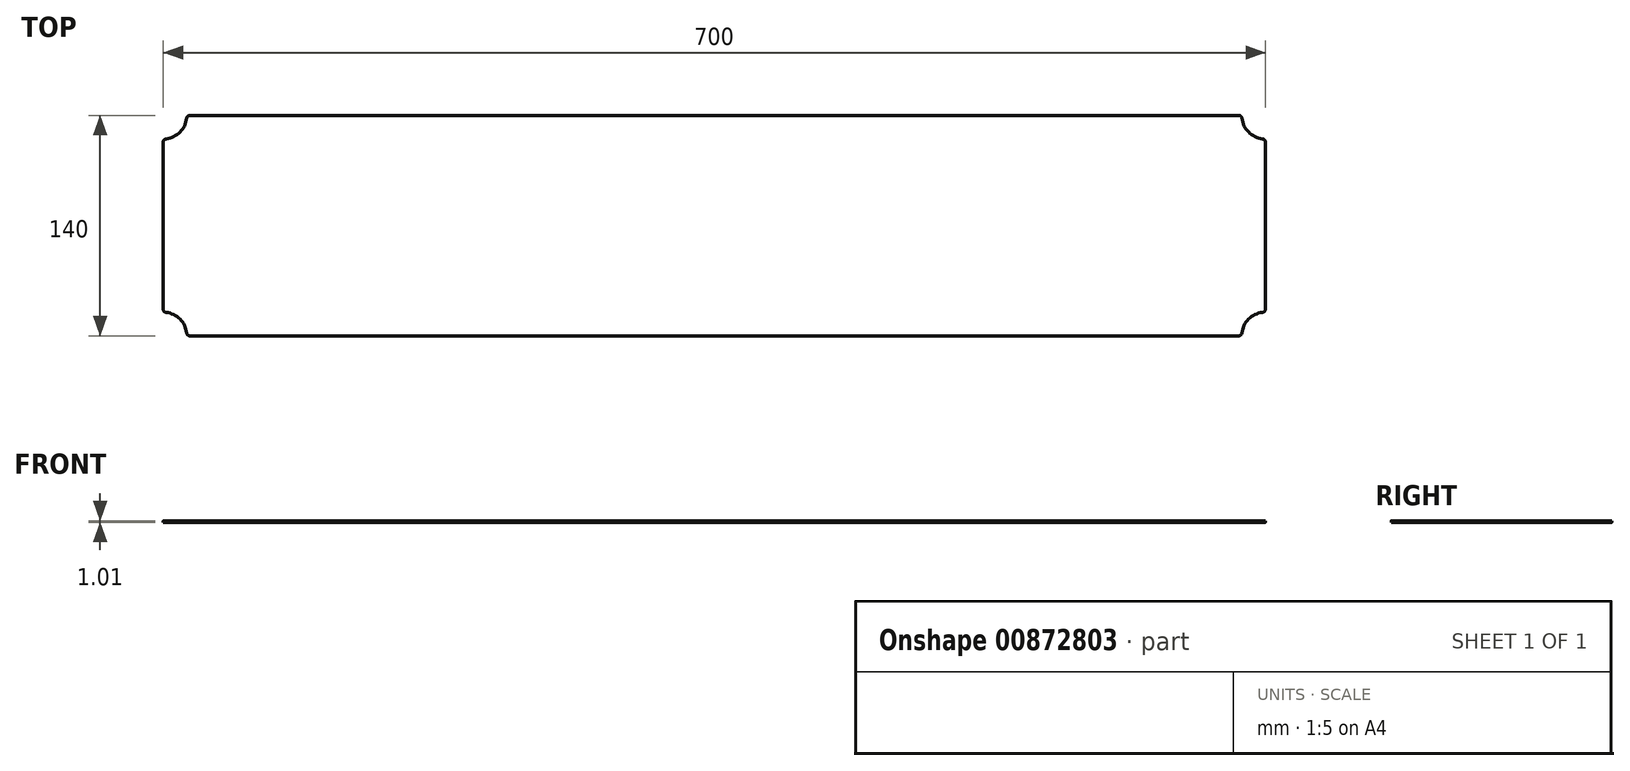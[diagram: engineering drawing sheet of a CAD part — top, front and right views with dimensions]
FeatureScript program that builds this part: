
annotation { "Feature Type Name" : "Feature", "Feature Type Description" : "" }
export const myFeature = defineFeature(function(context is Context, id is Id, definition is map)
    precondition{}
    {
        {
            var Q0;
            Q0=qCreatedBy(makeId("Top.planeOp"),FACE);
            var sketch = newSketch(context, id + "F0", { "sketchPlane" : qUnion([Q0])});
            skLineSegment(sketch, "E0.bottom", {"start": v(-333.12, 70) * mm, "end": v(0, 70) * mm});
            skLineSegment(sketch, "E0.top", {"start": v(-350, 0) * mm, "end": v(0, 0) * mm});
            skLineSegment(sketch, "E0.left", {"start": v(-350, 53.12) * mm, "end": v(-350, 0) * mm});
            skLineSegment(sketch, "E0.right", {"start": v(0, 70) * mm, "end": v(0, 0) * mm});
            skArc(sketch, "E1", {"start": v(-348.24, 55.1) * mm, "mid": v(-339.4, 59.4) * mm, "end": v(-335.1, 68.24) * mm});
            skLineSegment(sketch, "E2.MirrorCS", {"start": v(350, 0) * mm, "end": v(0, 0) * mm});
            skLineSegment(sketch, "E3.MirrorCS", {"start": v(333.12, 70) * mm, "end": v(0, 70) * mm});
            skLineSegment(sketch, "E4.MirrorCS", {"start": v(350, 53.12) * mm, "end": v(350, 0) * mm});
            skArc(sketch, "E5.MirrorC", {"start": v(348.24, 55.1) * mm, "mid": v(339.4, 59.4) * mm, "end": v(335.1, 68.24) * mm});
            skLineSegment(sketch, "E6.MirrorCS", {"start": v(0, -70) * mm, "end": v(0, 0) * mm});
            skArc(sketch, "E7.MirrorC", {"start": v(-348.24, -55.1) * mm, "mid": v(-339.4, -59.4) * mm, "end": v(-335.1, -68.24) * mm});
            skLineSegment(sketch, "E8.MirrorCS", {"start": v(-333.12, -70) * mm, "end": v(0, -70) * mm});
            skLineSegment(sketch, "E9.MirrorCS", {"start": v(-350, -53.12) * mm, "end": v(-350, 0) * mm});
            skLineSegment(sketch, "E10.MirrorCS", {"start": v(350, -53.12) * mm, "end": v(350, 0) * mm});
            skLineSegment(sketch, "E11.MirrorCS", {"start": v(333.12, -70) * mm, "end": v(0, -70) * mm});
            skArc(sketch, "E12.MirrorC", {"start": v(348.24, -55.1) * mm, "mid": v(339.4, -59.4) * mm, "end": v(335.1, -68.24) * mm});
            skPoint(sketch, "E13.visualSharp", {"position": v(-335, 70) * mm});
            skArc(sketch, "E13.filletArc", {"start": v(-333.12, 70) * mm, "mid": v(-334.45, 69.5) * mm, "end": v(-335.1, 68.24) * mm});
            skPoint(sketch, "E14.visualSharp", {"position": v(-350, 55) * mm});
            skArc(sketch, "E14.filletArc", {"start": v(-348.24, 55.1) * mm, "mid": v(-349.5, 54.45) * mm, "end": v(-350, 53.12) * mm});
            skPoint(sketch, "E15.visualSharp", {"position": v(-350, -55) * mm});
            skArc(sketch, "E15.filletArc", {"start": v(-350, -53.12) * mm, "mid": v(-349.5, -54.45) * mm, "end": v(-348.24, -55.1) * mm});
            skPoint(sketch, "E16.visualSharp", {"position": v(-335, -70) * mm});
            skArc(sketch, "E16.filletArc", {"start": v(-335.1, -68.24) * mm, "mid": v(-334.45, -69.5) * mm, "end": v(-333.12, -70) * mm});
            skPoint(sketch, "E17.visualSharp", {"position": v(335, 70) * mm});
            skArc(sketch, "E17.filletArc", {"start": v(335.1, 68.24) * mm, "mid": v(334.45, 69.5) * mm, "end": v(333.12, 70) * mm});
            skPoint(sketch, "E18.visualSharp", {"position": v(350, 55) * mm});
            skArc(sketch, "E18.filletArc", {"start": v(350, 53.12) * mm, "mid": v(349.5, 54.45) * mm, "end": v(348.24, 55.1) * mm});
            skPoint(sketch, "E19.visualSharp", {"position": v(350, -55) * mm});
            skArc(sketch, "E19.filletArc", {"start": v(348.24, -55.1) * mm, "mid": v(349.5, -54.45) * mm, "end": v(350, -53.12) * mm});
            skPoint(sketch, "E20.visualSharp", {"position": v(335, -70) * mm});
            skArc(sketch, "E20.filletArc", {"start": v(333.12, -70) * mm, "mid": v(334.45, -69.5) * mm, "end": v(335.1, -68.24) * mm});
            skSolve(sketch);
        }
        {
            var Q0;
            Q0=qSketchRegion(id+"F0",true);
            extrude(context, id + "F1", {"entities" : qUnion([Q0]), "depth" : 1.01 * mm, "offsetDistance" : 25 * mm});
        }
    });
